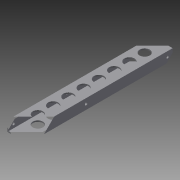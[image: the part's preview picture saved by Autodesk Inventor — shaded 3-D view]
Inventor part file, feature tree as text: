
AUTODESK INVENTOR PART (.ipt)
format: ipt  version: 2015 (Build 190159000, 159)  size: 147,456 bytes
history: native  units: in
note: dims shown in document units (in); Inventor stores cm internally (conversion verified against a paired STEP export)
features: sketch x4, hole x3, projected_geometry x3, extrude x1, pattern_linear x1
ambient origin geometry x8: Origin, YZ Plane, XZ Plane, XY Plane, X Axis, Y Axis, Z Axis, Center Point
bodies: Solid1 (feature_tree)
feature tree (12):
  extrude  "Extrusion1"  Depth=1.0in
  hole  "Hole1"  [1 undecoded]
  hole  "Hole2"  [1 undecoded]
  hole  "Hole3"  [1 undecoded]
  pattern_linear  "Rectangular Pattern1"  Spacing1=0.5in  [1 undecoded]
  sketch  "Sketch1"  dims[d0=2.0in d1=1.0in]
  sketch  "Sketch2"  dims[d2=1.75in d3=0.75in]
  projected_geometry  "Projected Loop1"
  sketch  "Sketch3"  dims[d4=0.125in d5=0.125in]
  projected_geometry  "Projected Loop2"
  sketch  "Sketch4"  dims[d6=14.25in d7=0.0in d8=0.5in d9=0.5in d10=8.5in d11=0.5in d12=0.25in d13=0.75in d14=0.375in d15=0.25in d16=0.5635in d17=1.0in d18=0.8108in d19=0.5in d20=0.5in d21=0.25in d22=0.75in d23=0.375in d24=0.25in d25=0.5635in d26=1.0in d27=0.8108in d28=1.0in d29=2.0in d30=1.0in d31=0.75in d32=0.375in d33=0.25in d34=0.5635in d35=1.0in d36=0.8108in d37=3.1496in d39=1.5in]
  projected_geometry  "Projected Loop3"
note: 4 required parameter values undecoded (feature->parameter linkage not recoverable at this tier; creation-order binding heuristic only, values carry confidence <= 0.55)
